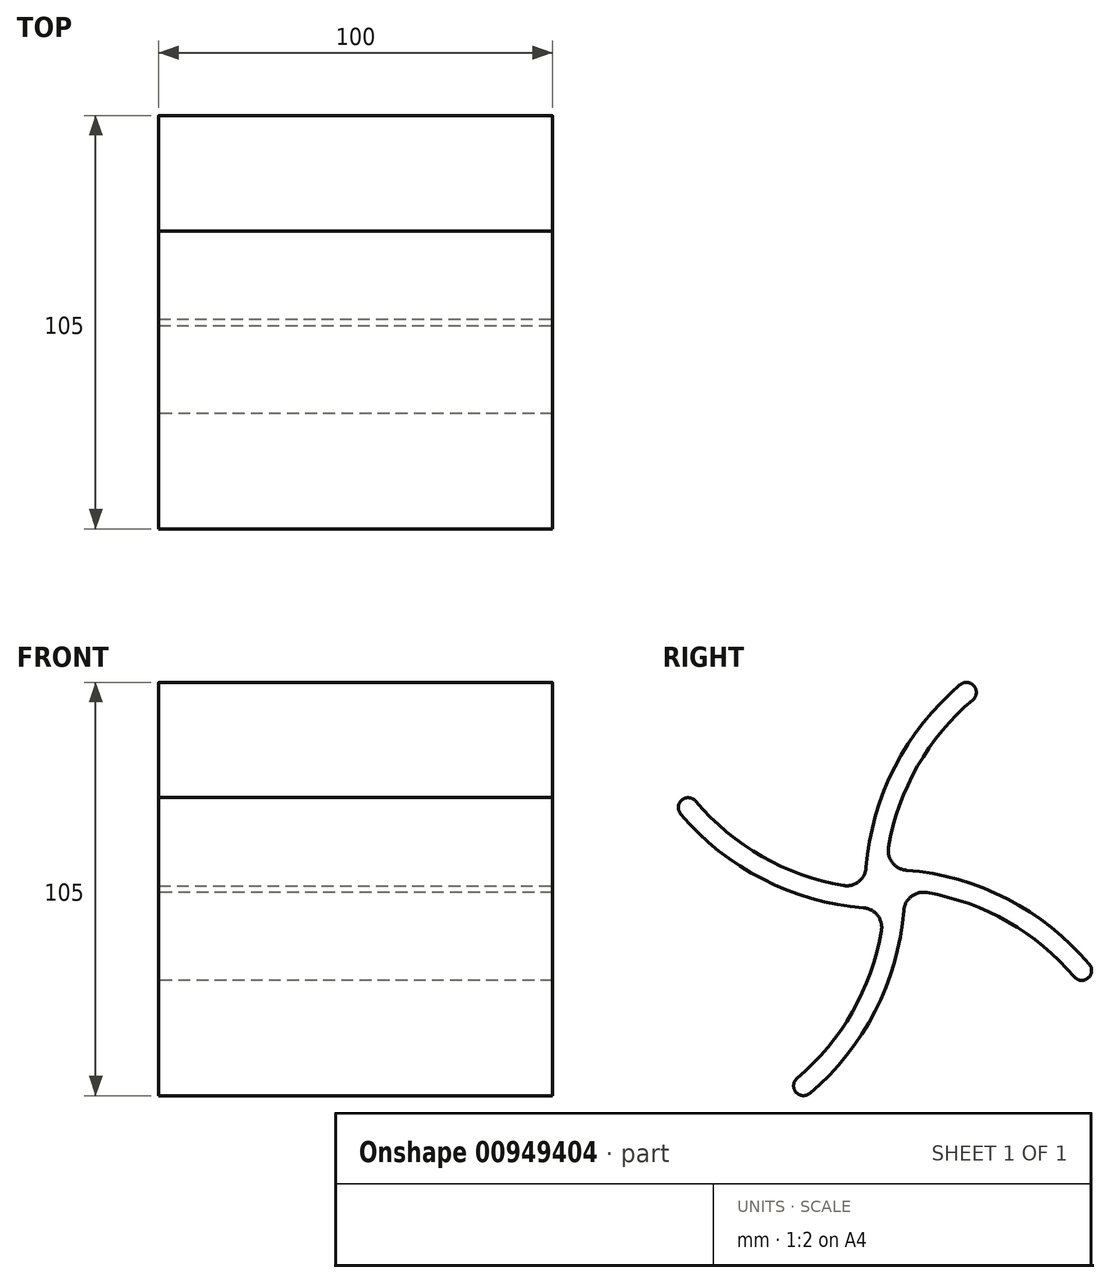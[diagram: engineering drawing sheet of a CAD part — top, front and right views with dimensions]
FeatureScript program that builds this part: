
annotation { "Feature Type Name" : "Feature", "Feature Type Description" : "" }
export const myFeature = defineFeature(function(context is Context, id is Id, definition is map)
    precondition{}
    {
        {
            var Q0;
            Q0=qCreatedBy(makeId("Right.planeOp"),FACE);
            var sketch = newSketch(context, id + "F0", { "sketchPlane" : qUnion([Q0])});
            skCircle(sketch, "E0.cCircle", {"center": v(0, 0) * mm, "radius": 50 * mm, "construction": true});
            skLineSegment(sketch, "E0.0", {"start": v(-20.71, 50) * mm, "end": v(20.71, 50) * mm, "construction": true});
            skLineSegment(sketch, "E0.1", {"start": v(20.71, 50) * mm, "end": v(50, 20.71) * mm, "construction": true});
            skLineSegment(sketch, "E0.2", {"start": v(50, 20.71) * mm, "end": v(50, -20.71) * mm, "construction": true});
            skLineSegment(sketch, "E0.3", {"start": v(50, -20.71) * mm, "end": v(20.71, -50) * mm, "construction": true});
            skLineSegment(sketch, "E0.4", {"start": v(20.71, -50) * mm, "end": v(-20.71, -50) * mm, "construction": true});
            skLineSegment(sketch, "E0.5", {"start": v(-20.71, -50) * mm, "end": v(-50, -20.71) * mm, "construction": true});
            skLineSegment(sketch, "E0.6", {"start": v(-50, -20.71) * mm, "end": v(-50, 20.71) * mm, "construction": true});
            skLineSegment(sketch, "E0.7", {"start": v(-50, 20.71) * mm, "end": v(-20.71, 50) * mm, "construction": true});
            skPoint(sketch, "E0.0.midPoint", {"position": v(0, 50) * mm});
            skArc(sketch, "E1", {"start": v(48.1, -22.32) * mm, "mid": v(26.5, -5.85) * mm, "end": v(0, 0) * mm});
            skArc(sketch, "E2", {"start": v(0, 5) * mm, "mid": v(28.62, -1.32) * mm, "end": v(51.9, -19.1) * mm});
            skArc(sketch, "E3", {"start": v(51.9, -19.1) * mm, "mid": v(51.61, -22.62) * mm, "end": v(48.1, -22.32) * mm});
            skCircle(sketch, "E4", {"center": v(0, 0) * mm, "radius": 5 * mm});
            skSolve(sketch);
        }
        {
            var Q0;
            Q0 = qSketchRegion(id + "F0", true);
            extrude(context, id + "F1", {"entities" : qUnion([Q0]), "endBound" : BoundingType.SYMMETRIC, "depth" : 100 * mm, "offsetDistance" : 25 * mm});
        }
        {
            var Q0;
            Q0=qCreatedBy(makeId("Top.planeOp"),FACE);
            var sketch = newSketch(context, id + "F2", { "sketchPlane" : qUnion([Q0])});
            skLineSegment(sketch, "E5", {"start": v(0, 0) * mm, "end": v(40.18, 0) * mm});
            skSolve(sketch);
        }
        {
            var Q0;
            Q0=makeQuery(id+"F1.opExtrude","SWEPT_BODY",BODY,{"disambiguationData":[OSD([sQuery(id+"F0.wireOp",EDGE,"E1"),sQuery(id+"F0.wireOp",EDGE,"E2"),sQuery(id+"F0.wireOp",EDGE,"E3"),sQuery(id+"F0.wireOp",EDGE,"E4")])]});
            var Q1;
            Q1=sQuery(id+"F2.wireOp",EDGE,"E5");
            circularPattern(context, id + "F3", {"operationType" : NewBodyOperationType.ADD, "entities" : qUnion([Q0]), "axis" : qUnion([Q1]), "angle" : 360 * degree, "instanceCount" : 4, "equalSpace" : true});
        }
        {
            var Q0;
            Q0=makeQuery(id+"F3.boolean.opBoolean","INTERSECT",EDGE,{"derivedFrom":[makeQuery(id+"F1.opExtrude","SWEPT_FACE",FACE,{"disambiguationData":[OSD([sQuery(id+"F0.wireOp",EDGE,"E1")])]}),makeQuery(id+"F3.opPattern","COPY",FACE,{"derivedFrom":makeQuery(id+"F1.opExtrude","SWEPT_FACE",FACE,{"disambiguationData":[OSD([sQuery(id+"F0.wireOp",EDGE,"E2")])]}),"instanceName":"3"})]});
            var Q1;
            Q1=makeQuery(id+"F3.boolean.opBoolean","INTERSECT",EDGE,{"derivedFrom":[makeQuery(id+"F3.opPattern","COPY",FACE,{"derivedFrom":makeQuery(id+"F1.opExtrude","SWEPT_FACE",FACE,{"disambiguationData":[OSD([sQuery(id+"F0.wireOp",EDGE,"E2")])]}),"instanceName":"2"}),makeQuery(id+"F3.opPattern","COPY",FACE,{"derivedFrom":makeQuery(id+"F1.opExtrude","SWEPT_FACE",FACE,{"disambiguationData":[OSD([sQuery(id+"F0.wireOp",EDGE,"E1")])]}),"instanceName":"3"})]});
            var Q2;
            Q2=makeQuery(id+"F3.boolean.opBoolean","INTERSECT",EDGE,{"derivedFrom":[makeQuery(id+"F3.opPattern","COPY",FACE,{"derivedFrom":makeQuery(id+"F1.opExtrude","SWEPT_FACE",FACE,{"disambiguationData":[OSD([sQuery(id+"F0.wireOp",EDGE,"E2")])]}),"instanceName":"1"}),makeQuery(id+"F3.opPattern","COPY",FACE,{"derivedFrom":makeQuery(id+"F1.opExtrude","SWEPT_FACE",FACE,{"disambiguationData":[OSD([sQuery(id+"F0.wireOp",EDGE,"E1")])]}),"instanceName":"2"})]});
            var Q3;
            Q3=makeQuery(id+"F3.boolean.opBoolean","INTERSECT",EDGE,{"derivedFrom":[makeQuery(id+"F1.opExtrude","SWEPT_FACE",FACE,{"disambiguationData":[OSD([sQuery(id+"F0.wireOp",EDGE,"E2")])]}),makeQuery(id+"F3.opPattern","COPY",FACE,{"derivedFrom":makeQuery(id+"F1.opExtrude","SWEPT_FACE",FACE,{"disambiguationData":[OSD([sQuery(id+"F0.wireOp",EDGE,"E1")])]}),"instanceName":"1"})]});
            fillet(context, id + "F4", {"entities" : qUnion([Q0, Q1, Q2, Q3]), "radius" : 5 * mm, "tangentPropagation" : true, "allowEdgeOverflow" : false});
        }
    });
